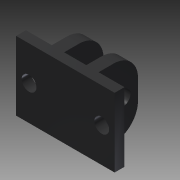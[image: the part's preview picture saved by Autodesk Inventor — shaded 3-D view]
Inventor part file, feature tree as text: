
AUTODESK INVENTOR PART (.ipt)
format: ipt  version: 2016 (Build 200138000, 138)  size: 151,040 bytes
history: native  units: mm
features: extrude x3, sketch x3, fillet x1
ambient origin geometry x8: Origin, YZ Plane, XZ Plane, XY Plane, X Axis, Y Axis, Z Axis, Center Point
bodies: Solid1 (feature_tree)
feature tree (7):
  extrude  "Extrusion1"  Depth=2.5mm
  extrude  "Extrusion2"  Depth=20.0mm
  fillet  "Fillet1"  Radius=5.25mm
  extrude  "Extrusion3"  Depth=14.0mm
  sketch  "Sketch1"  dims[d0=4.5mm d3=2.5mm]
  sketch  "Sketch2"  dims[d5=2.5mm d7=20.0mm d8=5.25mm]
  sketch  "Sketch3"  dims[d9=5.25mm d10=14.0mm d11=3.0mm d12=3.0mm d13=2.0mm d14=0.0mm d16=4.5mm d17=2.5mm d18=2.5mm d19=8.0mm d20=0.0mm d21=5.0mm d23=3.0mm d24=5.0mm d25=20.0mm d26=0.0mm d27=2.625mm d28=2.625mm d29=2.625mm]
